# Revit family: EV4D-02WAL
name_source: partatom
category: Lighting Fixtures
revit_build: Autodesk Revit 2014 (Build: 20130308_1515(x64)
units: mm (PartAtom-declared; Revit-internal decimal feet)

## types (2) — shared parameters
Color Filter = 16777215
Compliances = Listed to UL924 Standard, NFPA 101, NFPA 70
RoHS
Default Elevation = 48 "
Description = The EV4D-02WAL is a compact architectural emergency light with an optimized lighting pattern which offers 50' spacing at a 7.5' mounting height.
Dimming Lamp Color Temperature Shift = <None>
LED = Paint - Hubbell - Green Textured
Lamp = LED
Manufacturer = Dual Lite
Model = EV4D-02WAL
Photometric Web File = EV4D-02WAL[1].IES
Photometric Web Link = https://www.hubbell.com
Product Documentation Link = https://hubbellcdn.com
Product Page URL = https://www.hubbell.com
Steel = Metal-Hubbell-Galvanized_Steel
Tilt Angle = 0.00°
Type Comments = Architectural LED Emergency Light
URL = https://www.hubbell.com
Warranty = LED Lifetime Warranty
EV Full 3 year warranty
EV with Spectron® Full 5 year warranty
Wattage Comments = 2W

## per-type parameters (varying)
| type | Body |
| White Housing | Paint - Hubbell - Matte White |
| Black Housing | Paint - Hubbell - Carbon Black |

## geometry (parser evidence)
native form markers: Sweep x2
no freeform markers — native parametric forms only
